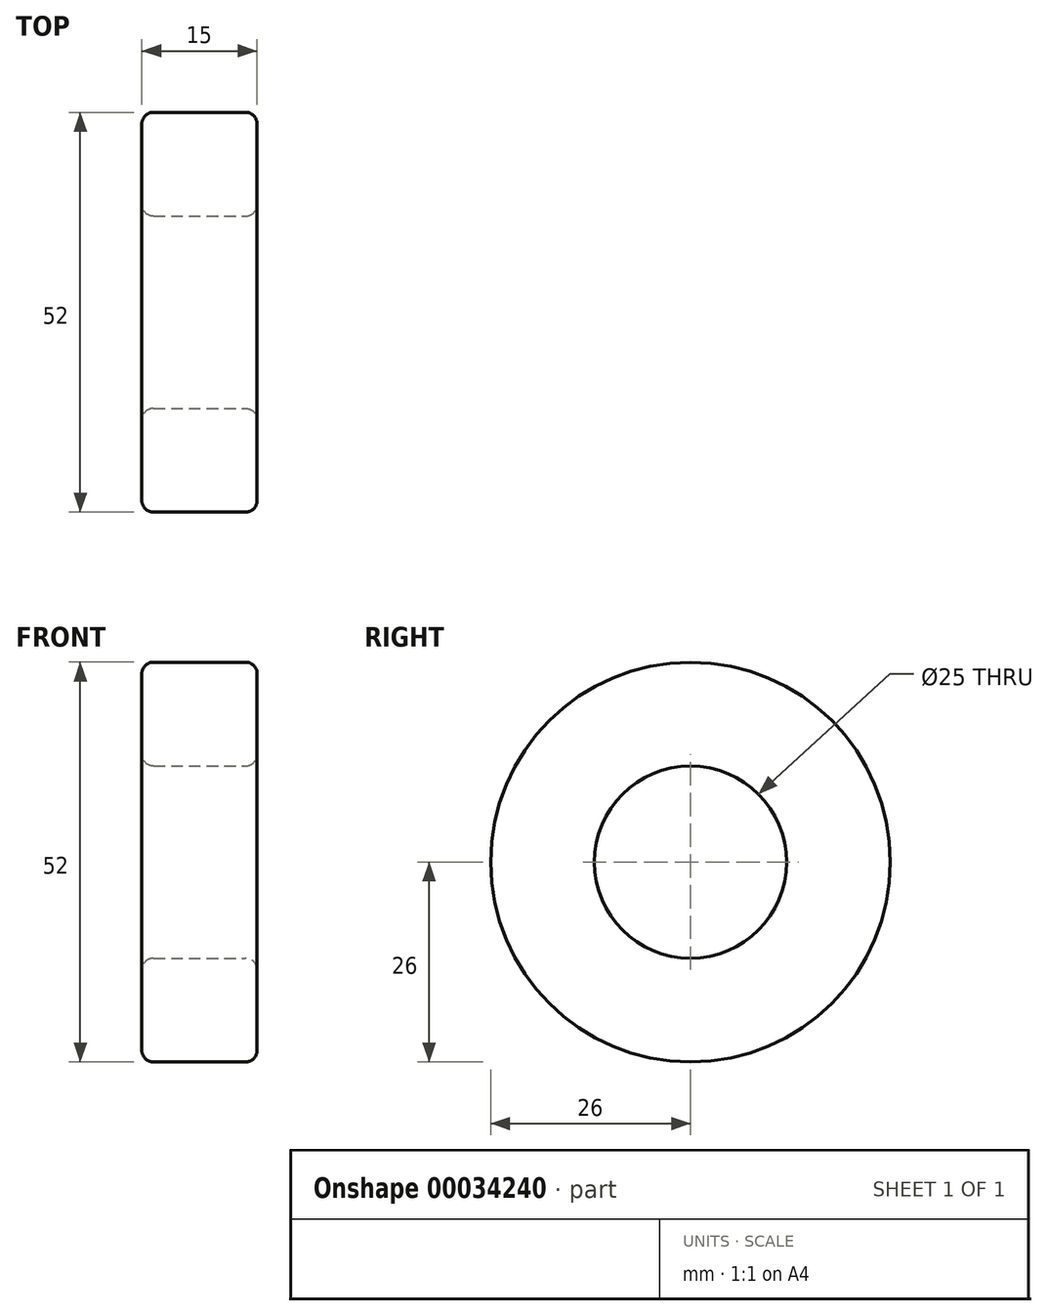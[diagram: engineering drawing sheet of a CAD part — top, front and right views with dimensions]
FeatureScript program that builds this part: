
annotation { "Feature Type Name" : "Feature", "Feature Type Description" : "" }
export const myFeature = defineFeature(function(context is Context, id is Id, definition is map)
    precondition{}
    {
        {
            var Q0;
            Q0=qCreatedBy(makeId("Right.planeOp"),FACE);
            var sketch = newSketch(context, id + "F0", { "sketchPlane" : qUnion([Q0])});
            skCircle(sketch, "E0", {"center": v(0, 0) * mm, "radius": 12.5 * mm});
            skCircle(sketch, "E1", {"center": v(0, 0) * mm, "radius": 26 * mm});
            skSolve(sketch);
        }
        {
            var Q0;
            Q0=makeQuery(id+"F0.imprint","IMPRINT",FACE,{"disambiguationData":[TD([[makeQuery(id+"F0.imprint","IMPRINT",EDGE,{"derivedFrom":sQuery(id+"F0.wireOp",EDGE,"E0")}),-1.0]])]});
            extrude(context, id + "F1", {"entities" : qUnion([Q0]), "oppositeDirection" : true, "depth" : 15 * mm});
        }
        {
            var Q0;
            Q0=makeQuery(id+"F1.opExtrude","CAP_FACE",FACE,{"disambiguationData":[OSD([sQuery(id+"F0.wireOp",EDGE,"E0"),sQuery(id+"F0.wireOp",EDGE,"E1")])],"isStart":true});
            var Q1;
            Q1=makeQuery(id+"F1.opExtrude","CAP_FACE",FACE,{"disambiguationData":[OSD([sQuery(id+"F0.wireOp",EDGE,"E0"),sQuery(id+"F0.wireOp",EDGE,"E1")])],"isStart":false});
            fillet(context, id + "F2", {"entities" : qUnion([Q0, Q1]), "radius" : 1.52 * mm, "tangentPropagation" : true, "allowEdgeOverflow" : false});
        }
    });
